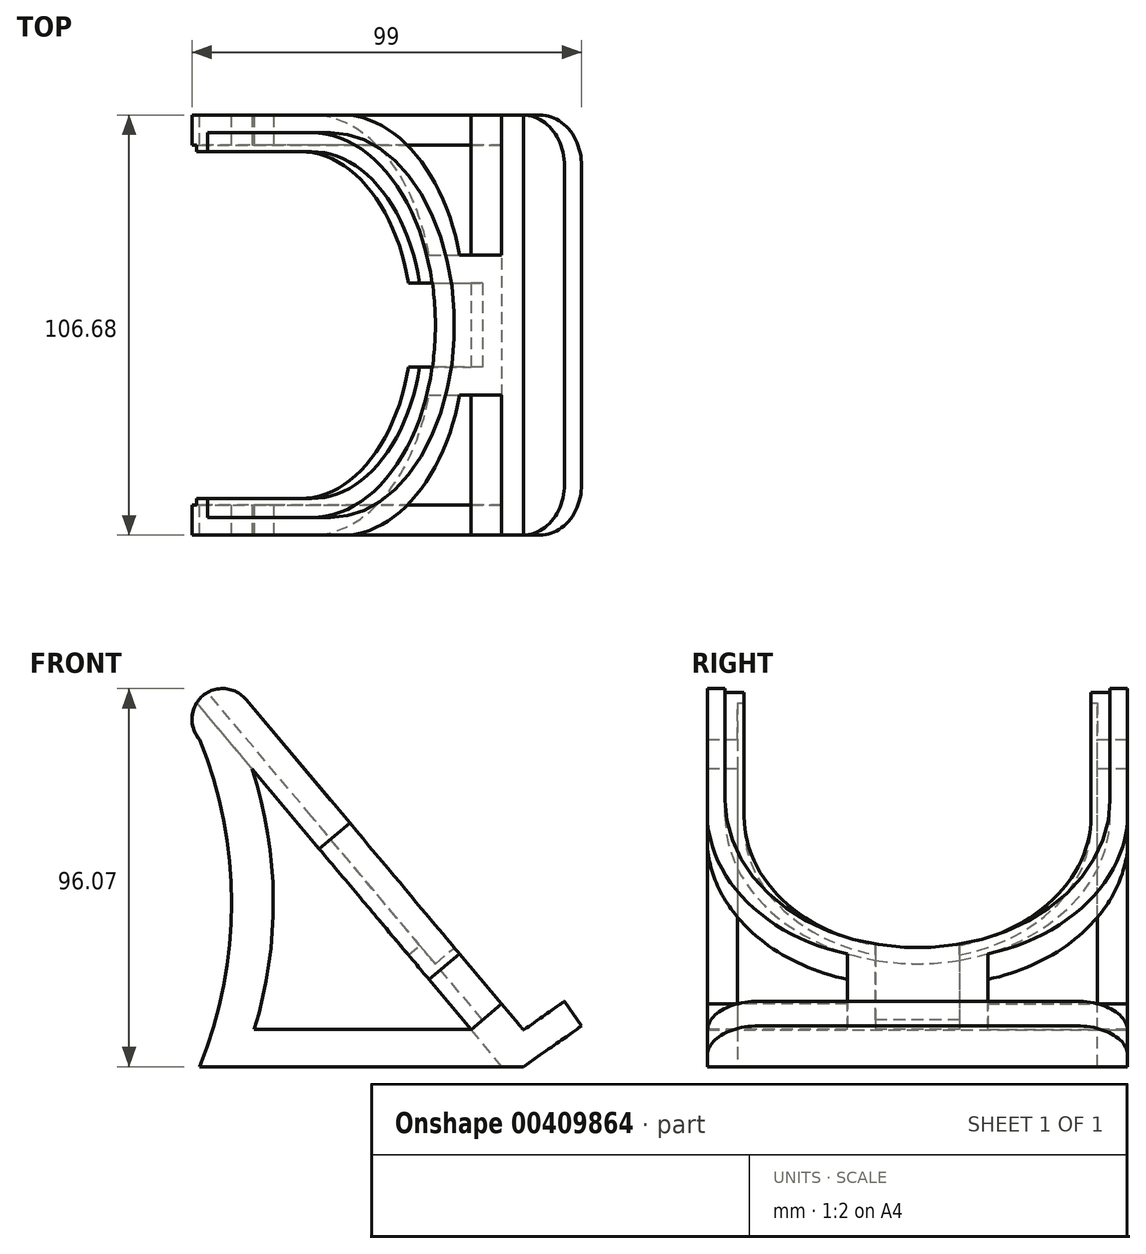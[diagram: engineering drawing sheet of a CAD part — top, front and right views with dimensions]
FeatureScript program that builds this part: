
annotation { "Feature Type Name" : "Feature", "Feature Type Description" : "" }
export const myFeature = defineFeature(function(context is Context, id is Id, definition is map)
    precondition{}
    {
        {
            var Q0;
            Q0=qCreatedBy(makeId("Front.planeOp"),FACE);
            var sketch = newSketch(context, id + "F0", { "sketchPlane" : qUnion([Q0])});
            skLineSegment(sketch, "E0", {"start": v(-26.46, -52) * mm, "end": v(55.88, -52) * mm});
            skLineSegment(sketch, "E1", {"start": v(55.88, -52) * mm, "end": v(70.65, -41.63) * mm});
            skLineSegment(sketch, "E2", {"start": v(70.65, -41.63) * mm, "end": v(66.27, -35.4) * mm});
            skLineSegment(sketch, "E3", {"start": v(66.27, -35.4) * mm, "end": v(55.88, -42.68) * mm});
            skLineSegment(sketch, "E4", {"start": v(55.88, -42.68) * mm, "end": v(-14.6, 41.3) * mm});
            skArc(sketch, "E5", {"start": v(-26.46, -52) * mm, "mid": v(-18.29, -10.4) * mm, "end": v(-26.46, 31.2) * mm});
            skArc(sketch, "E6", {"start": v(-14.6, 41.3) * mm, "mid": v(-25.6, 42.22) * mm, "end": v(-26.46, 31.2) * mm});
            skSolve(sketch);
        }
        {
            var Q0;
            Q0=makeQuery(id+"F0.imprint","IMPRINT",FACE,{"disambiguationData":[TD([[makeQuery(id+"F0.imprint","IMPRINT",EDGE,{"derivedFrom":sQuery(id+"F0.wireOp",EDGE,"E0")}),1.0]])]});
            var Q1;
            Q1=qSketchRegion(id+"F2",true);
            extrude(context, id + "F1", {"entities" : qUnion([Q0, Q1]), "endBound" : BoundingType.SYMMETRIC, "depth" : 106.68 * mm});
        }
        {
            var Q0;
            Q0=makeQuery(id+"F1.opExtrude","SWEPT_FACE",FACE,{"disambiguationData":[OSD([sQuery(id+"F0.wireOp",EDGE,"E4")])]});
            var sketch = newSketch(context, id + "F2", { "sketchPlane" : qUnion([Q0])});
            skCircle(sketch, "E7", {"center": v(0, 7.58) * mm, "radius": 48.9 * mm});
            skLineSegment(sketch, "E8", {"start": v(0, 7.58) * mm, "end": v(-48.9, 7.58) * mm, "construction": true});
            skLineSegment(sketch, "E9", {"start": v(-48.9, 7.58) * mm, "end": v(-48.9, 73.2) * mm});
            skLineSegment(sketch, "E10", {"start": v(-48.9, 73.2) * mm, "end": v(0, 73.2) * mm});
            skLineSegment(sketch, "E11", {"start": v(0, 73.2) * mm, "end": v(0, 7.58) * mm});
            skLineSegment(sketch, "E12", {"start": v(-48.9, 7.58) * mm, "end": v(0, 7.58) * mm});
            skLineSegment(sketch, "E13.MirrorCS", {"start": v(46.05, 73.08) * mm, "end": v(0, 73.2) * mm});
            skLineSegment(sketch, "E14", {"start": v(-6.35, -68.84) * mm, "end": v(6.35, -68.84) * mm});
            skCircle(sketch, "E15", {"center": v(0, 7.58) * mm, "radius": 44.07 * mm});
            skLineSegment(sketch, "E16", {"start": v(-44.07, 7.58) * mm, "end": v(-44.07, 73.2) * mm});
            skLineSegment(sketch, "E17.MirrorCS", {"start": v(44.07, 7.58) * mm, "end": v(44.07, 73.2) * mm});
            skArc(sketch, "E18", {"start": v(-53.34, 0) * mm, "mid": v(-42.03, -27.71) * mm, "end": v(-16.69, -43.64) * mm});
            skLineSegment(sketch, "E19", {"start": v(-17.83, -43.33) * mm, "end": v(-17.83, -59.96) * mm});
            skLineSegment(sketch, "E20", {"start": v(-17.83, -59.96) * mm, "end": v(-53.34, -59.96) * mm});
            skLineSegment(sketch, "E21", {"start": v(-53.34, -59.96) * mm, "end": v(-53.34, 0) * mm});
            skArc(sketch, "E22.MirrorCS", {"start": v(53.34, 0) * mm, "mid": v(42.03, -27.71) * mm, "end": v(16.69, -43.64) * mm});
            skLineSegment(sketch, "E23.MirrorCS", {"start": v(17.83, -43.33) * mm, "end": v(17.83, -59.96) * mm});
            skLineSegment(sketch, "E24.MirrorCS", {"start": v(17.83, -59.96) * mm, "end": v(53.34, -59.96) * mm});
            skLineSegment(sketch, "E25.MirrorCS", {"start": v(53.34, -59.96) * mm, "end": v(53.34, 0) * mm});
            skLineSegment(sketch, "E26.MirrorCS", {"start": v(48.9, 7.58) * mm, "end": v(48.9, 73.2) * mm});
            skLineSegment(sketch, "E27.MirrorCS", {"start": v(48.9, 73.2) * mm, "end": v(0, 73.2) * mm});
            skSolve(sketch);
        }
        {
            var Q0;
            {var subQ1=sQuery(id+"F2.wireOp",EDGE,"E7");var subQ3=sQuery(id+"F2.wireOp",EDGE,"E16");var subQ4=makeQuery(id+"F2.imprint","INTERSECT",VERTEX,{"derivedFrom":[subQ1,subQ3]});Q0=makeQuery(id+"F2.imprint","IMPRINT",FACE,{"disambiguationData":[TD([[makeQuery(id+"F2.imprint","IMPRINT",EDGE,{"disambiguationData":[TD([[subQ4,-1.0]])],"derivedFrom":subQ1}),1.0]])]});}
            var Q1;
            {var subQ0=sQuery(id+"F2.wireOp",EDGE,"E17.MirrorCS");var subQ1=sQuery(id+"F2.wireOp",EDGE,"E7");var subQ2=makeQuery(id+"F2.imprint","INTERSECT",VERTEX,{"derivedFrom":[subQ1,subQ0]});Q1=makeQuery(id+"F2.imprint","IMPRINT",FACE,{"disambiguationData":[TD([[makeQuery(id+"F2.imprint","IMPRINT",EDGE,{"disambiguationData":[TD([[subQ2,1.0]])],"derivedFrom":subQ1}),-1.0]])]});}
            var Q2;
            {var subQ0=sQuery(id+"F2.wireOp",EDGE,"E11");var subQ3=sQuery(id+"F2.wireOp",EDGE,"E7");var subQ4=makeQuery(id+"F2.imprint","INTERSECT",VERTEX,{"derivedFrom":[subQ3,subQ0]});Q2=makeQuery(id+"F2.imprint","IMPRINT",FACE,{"disambiguationData":[TD([[makeQuery(id+"F2.imprint","IMPRINT",EDGE,{"disambiguationData":[TD([[subQ4,-1.0]])],"derivedFrom":subQ3}),-1.0]])]});}
            var Q3;
            {var subQ0=sQuery(id+"F2.wireOp",EDGE,"E10");var subQ1=sQuery(id+"F2.wireOp",EDGE,"E9");var subQ2=makeQuery(id+"F2.imprint","INTERSECT",VERTEX,{"derivedFrom":[subQ1,subQ0]});Q3=makeQuery(id+"F2.imprint","IMPRINT",FACE,{"disambiguationData":[TD([[makeQuery(id+"F2.imprint","IMPRINT",EDGE,{"disambiguationData":[TD([[subQ2,-1.0]])],"derivedFrom":subQ0}),-1.0]])]});}
            var Q4;
            {var subQ0=sQuery(id+"F2.wireOp",EDGE,"E13.MirrorCS");var subQ1=sQuery(id+"F2.wireOp",EDGE,"4d85ec23-4223-449c-91b3-d977c7df0c140.MirrorCS");var subQ2=makeQuery(id+"F2.imprint","INTERSECT",VERTEX,{"derivedFrom":[subQ1,subQ0]});Q4=makeQuery(id+"F2.imprint","IMPRINT",FACE,{"disambiguationData":[TD([[makeQuery(id+"F2.imprint","IMPRINT",EDGE,{"disambiguationData":[TD([[subQ2,-1.0]])],"derivedFrom":subQ0}),1.0]])]});}
            var Q5;
            {var subQ0=sQuery(id+"F2.wireOp",EDGE,"E11");var subQ1=sQuery(id+"F2.wireOp",EDGE,"E7");var subQ2=makeQuery(id+"F2.imprint","INTERSECT",VERTEX,{"derivedFrom":[subQ1,subQ0]});Q5=makeQuery(id+"F2.imprint","IMPRINT",FACE,{"disambiguationData":[TD([[makeQuery(id+"F2.imprint","IMPRINT",EDGE,{"disambiguationData":[TD([[subQ2,-1.0]])],"derivedFrom":subQ1}),1.0]])]});}
            var Q6;
            {var subQ0=sQuery(id+"F2.wireOp",EDGE,"E11");var subQ1=sQuery(id+"F2.wireOp",EDGE,"E7");var subQ2=makeQuery(id+"F2.imprint","INTERSECT",VERTEX,{"derivedFrom":[subQ1,subQ0]});Q6=makeQuery(id+"F2.imprint","IMPRINT",FACE,{"disambiguationData":[TD([[makeQuery(id+"F2.imprint","IMPRINT",EDGE,{"disambiguationData":[TD([[subQ2,1.0]])],"derivedFrom":subQ1}),1.0]])]});}
            var Q7;
            {var subQ1=sQuery(id+"F2.wireOp",EDGE,"E7");var subQ3=sQuery(id+"F2.wireOp",EDGE,"E16");var subQ4=makeQuery(id+"F2.imprint","INTERSECT",VERTEX,{"derivedFrom":[subQ1,subQ3]});Q7=makeQuery(id+"F2.imprint","IMPRINT",FACE,{"disambiguationData":[TD([[makeQuery(id+"F2.imprint","IMPRINT",EDGE,{"disambiguationData":[TD([[subQ4,-1.0]])],"derivedFrom":subQ1}),-1.0]])]});}
            var Q8;
            {var subQ5=sQuery(id+"F2.wireOp",EDGE,"E11");var subQ7=sQuery(id+"F2.wireOp",EDGE,"E7");var subQ8=makeQuery(id+"F2.imprint","INTERSECT",VERTEX,{"derivedFrom":[subQ7,subQ5]});Q8=makeQuery(id+"F2.imprint","IMPRINT",FACE,{"disambiguationData":[TD([[makeQuery(id+"F2.imprint","IMPRINT",EDGE,{"disambiguationData":[TD([[subQ8,1.0]])],"derivedFrom":subQ7}),-1.0]])]});}
            var Q9;
            {var subQ0=sQuery(id+"F2.wireOp",EDGE,"E16");var subQ1=sQuery(id+"F2.wireOp",EDGE,"E7");var subQ2=makeQuery(id+"F2.imprint","INTERSECT",VERTEX,{"derivedFrom":[subQ1,subQ0]});Q9=makeQuery(id+"F2.imprint","IMPRINT",FACE,{"disambiguationData":[TD([[makeQuery(id+"F2.imprint","IMPRINT",EDGE,{"disambiguationData":[TD([[subQ2,1.0]])],"derivedFrom":subQ1}),-1.0]])]});}
            var Q10;
            {var subQ0=sQuery(id+"F2.wireOp",EDGE,"E16");var subQ3=sQuery(id+"F2.wireOp",EDGE,"E7");var subQ4=makeQuery(id+"F2.imprint","INTERSECT",VERTEX,{"derivedFrom":[subQ3,subQ0]});Q10=makeQuery(id+"F2.imprint","IMPRINT",FACE,{"disambiguationData":[TD([[makeQuery(id+"F2.imprint","IMPRINT",EDGE,{"disambiguationData":[TD([[subQ4,1.0]])],"derivedFrom":subQ3}),1.0]])]});}
            var Q11;
            {var subQ0=sQuery(id+"F2.wireOp",EDGE,"E17.MirrorCS");var subQ1=sQuery(id+"F2.wireOp",EDGE,"E15");var subQ2=makeQuery(id+"F2.imprint","INTERSECT",VERTEX,{"derivedFrom":[subQ1,subQ0]});Q11=makeQuery(id+"F2.imprint","IMPRINT",FACE,{"disambiguationData":[TD([[makeQuery(id+"F2.imprint","IMPRINT",EDGE,{"disambiguationData":[TD([[subQ2,-1.0]])],"derivedFrom":subQ1}),-1.0]])]});}
            var Q12;
            {var subQ0=sQuery(id+"F2.wireOp",EDGE,"E7");var subQ7=sQuery(id+"F2.wireOp",EDGE,"E17.MirrorCS");var subQ11=makeQuery(id+"F2.imprint","INTERSECT",VERTEX,{"derivedFrom":[subQ0,subQ7]});Q12=makeQuery(id+"F2.imprint","IMPRINT",FACE,{"disambiguationData":[TD([[makeQuery(id+"F2.imprint","IMPRINT",EDGE,{"disambiguationData":[TD([[subQ11,1.0]])],"derivedFrom":subQ0}),1.0]])]});}
            var Q13;
            {var subQ0=sQuery(id+"F2.wireOp",EDGE,"E12");var subQ1=sQuery(id+"F2.wireOp",EDGE,"E11");var subQ2=makeQuery(id+"F2.imprint","INTERSECT",VERTEX,{"derivedFrom":[subQ1,subQ0]});Q13=makeQuery(id+"F2.imprint","IMPRINT",FACE,{"disambiguationData":[TD([[makeQuery(id+"F2.imprint","IMPRINT",EDGE,{"disambiguationData":[TD([[subQ2,1.0]])],"derivedFrom":subQ1}),1.0]])]});}
            var Q14;
            {var subQ0=sQuery(id+"F2.wireOp",EDGE,"E12");var subQ1=sQuery(id+"F2.wireOp",EDGE,"E11");var subQ2=makeQuery(id+"F2.imprint","INTERSECT",VERTEX,{"derivedFrom":[subQ1,subQ0]});Q14=makeQuery(id+"F2.imprint","IMPRINT",FACE,{"disambiguationData":[TD([[makeQuery(id+"F2.imprint","IMPRINT",EDGE,{"disambiguationData":[TD([[subQ2,1.0]])],"derivedFrom":subQ1}),-1.0]])]});}
            var Q15;
            {var subQ0=sQuery(id+"F2.wireOp",EDGE,"E17.MirrorCS");var subQ1=sQuery(id+"F2.wireOp",EDGE,"E7");var subQ2=makeQuery(id+"F2.imprint","INTERSECT",VERTEX,{"derivedFrom":[subQ1,subQ0]});Q15=makeQuery(id+"F2.imprint","IMPRINT",FACE,{"disambiguationData":[TD([[makeQuery(id+"F2.imprint","IMPRINT",EDGE,{"disambiguationData":[TD([[subQ2,-1.0]])],"derivedFrom":subQ1}),-1.0]])]});}
            var Q16;
            {var subQ0=sQuery(id+"F2.wireOp",EDGE,"E27.MirrorCS");var subQ1=sQuery(id+"F2.wireOp",EDGE,"E17.MirrorCS");var subQ2=makeQuery(id+"F2.imprint","INTERSECT",VERTEX,{"derivedFrom":[subQ1,subQ0]});Q16=makeQuery(id+"F2.imprint","IMPRINT",FACE,{"disambiguationData":[TD([[makeQuery(id+"F2.imprint","IMPRINT",EDGE,{"disambiguationData":[TD([[subQ2,1.0]])],"derivedFrom":subQ1}),-1.0]])]});}
            extrude(context, id + "F3", {"entities" : qUnion([Q0, Q1, Q2, Q3, Q4, Q5, Q6, Q7, Q8, Q9, Q10, Q11, Q12, Q13, Q14, Q15, Q16]), "operationType" : NewBodyOperationType.REMOVE, "oppositeDirection" : true, "depth" : 6.35 * mm});
        }
        {
            var Q0;
            Q0=makeQuery(id+"F1.opExtrude","CAP_FACE",FACE,{"disambiguationData":[OSD([sQuery(id+"F0.wireOp",EDGE,"E0"),sQuery(id+"F0.wireOp",EDGE,"E1"),sQuery(id+"F0.wireOp",EDGE,"E2"),sQuery(id+"F0.wireOp",EDGE,"E3"),sQuery(id+"F0.wireOp",EDGE,"E4"),sQuery(id+"F0.wireOp",EDGE,"E5"),sQuery(id+"F0.wireOp",EDGE,"E6")])],"isStart":false});
            var sketch = newSketch(context, id + "F4", { "sketchPlane" : qUnion([Q0])});
            skLineSegment(sketch, "E28", {"start": v(-13.05, 23.66) * mm, "end": v(42.5, -42.55) * mm});
            skArc(sketch, "E29", {"start": v(-12.51, -42.55) * mm, "mid": v(-7.68, -9.4) * mm, "end": v(-13.05, 23.66) * mm});
            skLineSegment(sketch, "E30", {"start": v(-12.51, -42.55) * mm, "end": v(42.5, -42.55) * mm});
            skSolve(sketch);
        }
        {
            var Q0;
            Q0=makeQuery(id+"F4.imprint","IMPRINT",FACE,{"disambiguationData":[TD([[makeQuery(id+"F4.imprint","IMPRINT",EDGE,{"derivedFrom":sQuery(id+"F4.wireOp",EDGE,"E28")}),-1.0]])]});
            var Q1;
            Q1=makeQuery(id+"F4.imprint","IMPRINT",FACE,{"disambiguationData":[TD([[makeQuery(id+"F4.imprint","IMPRINT",EDGE,{"derivedFrom":sQuery(id+"F4.wireOp",EDGE,"wPjwQzWi-Tjyw-v6FZ-FHt0-rqqnCeeGMehr")}),-1.0]])]});
            extrude(context, id + "F5", {"entities" : qUnion([Q0, Q1]), "operationType" : NewBodyOperationType.REMOVE, "endBound" : BoundingType.UP_TO_NEXT, "oppositeDirection" : true, "depth" : 25.4 * mm});
        }
        {
            var Q0;
            Q0=makeQuery(id+"F1.opExtrude","SWEPT_EDGE",EDGE,{"disambiguationData":[OSD([sQuery(id+"F0.wireOp",EDGE,"E0"),sQuery(id+"F0.wireOp",EDGE,"E5")])]});
            cPlane(context, id + "F6", {"entities" : qUnion([Q0]), "cplaneType" : CPlaneType.LINE_ANGLE, "offset" : 40.4 * mm, "angle" : 50 * degree, "width" : 152.4 * mm, "height" : 152.4 * mm});
        }
        {
            var Q0;
            Q0=qCreatedBy(id+"F6.planeOp",FACE);
            var sketch = newSketch(context, id + "F7", { "sketchPlane" : qUnion([Q0])});
            skLineSegment(sketch, "E31", {"start": v(45.72, 83.56) * mm, "end": v(-45.72, 83.56) * mm});
            skLineSegment(sketch, "E32", {"start": v(-45.72, 83.56) * mm, "end": v(-45.72, -100.06) * mm});
            skLineSegment(sketch, "E33", {"start": v(-45.72, -100.06) * mm, "end": v(45.72, -100.06) * mm});
            skLineSegment(sketch, "E34", {"start": v(45.72, -100.06) * mm, "end": v(45.72, 83.56) * mm});
            skSolve(sketch);
        }
        {
            var Q0;
            Q0=makeQuery(id+"F7.imprint","IMPRINT",FACE,{"disambiguationData":[TD([[makeQuery(id+"F7.imprint","IMPRINT",EDGE,{"derivedFrom":sQuery(id+"F7.wireOp",EDGE,"E31")}),1.0]])]});
            extrude(context, id + "F8", {"entities" : qUnion([Q0]), "operationType" : NewBodyOperationType.REMOVE, "depth" : 58.93 * mm});
        }
        {
            var Q0;
            {var subQ0=sQuery(id+"F2.wireOp",EDGE,"E12");var subQ1=sQuery(id+"F2.wireOp",EDGE,"E11");var subQ2=makeQuery(id+"F2.imprint","INTERSECT",VERTEX,{"derivedFrom":[subQ1,subQ0]});Q0=makeQuery(id+"F2.imprint","IMPRINT",FACE,{"disambiguationData":[TD([[makeQuery(id+"F2.imprint","IMPRINT",EDGE,{"disambiguationData":[TD([[subQ2,1.0]])],"derivedFrom":subQ1}),-1.0]])]});}
            var Q1;
            {var subQ0=sQuery(id+"F2.wireOp",EDGE,"E12");var subQ1=sQuery(id+"F2.wireOp",EDGE,"E11");var subQ2=makeQuery(id+"F2.imprint","INTERSECT",VERTEX,{"derivedFrom":[subQ1,subQ0]});Q1=makeQuery(id+"F2.imprint","IMPRINT",FACE,{"disambiguationData":[TD([[makeQuery(id+"F2.imprint","IMPRINT",EDGE,{"disambiguationData":[TD([[subQ2,1.0]])],"derivedFrom":subQ1}),1.0]])]});}
            var Q2;
            {var subQ0=sQuery(id+"F2.wireOp",EDGE,"E16");var subQ3=sQuery(id+"F2.wireOp",EDGE,"E7");var subQ4=makeQuery(id+"F2.imprint","INTERSECT",VERTEX,{"derivedFrom":[subQ3,subQ0]});Q2=makeQuery(id+"F2.imprint","IMPRINT",FACE,{"disambiguationData":[TD([[makeQuery(id+"F2.imprint","IMPRINT",EDGE,{"disambiguationData":[TD([[subQ4,1.0]])],"derivedFrom":subQ3}),1.0]])]});}
            var Q3;
            {var subQ0=sQuery(id+"F2.wireOp",EDGE,"E17.MirrorCS");var subQ1=sQuery(id+"F2.wireOp",EDGE,"E15");var subQ2=makeQuery(id+"F2.imprint","INTERSECT",VERTEX,{"derivedFrom":[subQ1,subQ0]});Q3=makeQuery(id+"F2.imprint","IMPRINT",FACE,{"disambiguationData":[TD([[makeQuery(id+"F2.imprint","IMPRINT",EDGE,{"disambiguationData":[TD([[subQ2,-1.0]])],"derivedFrom":subQ1}),-1.0]])]});}
            var Q4;
            {var subQ0=sQuery(id+"F2.wireOp",EDGE,"E11");var subQ1=sQuery(id+"F2.wireOp",EDGE,"E7");var subQ2=makeQuery(id+"F2.imprint","INTERSECT",VERTEX,{"derivedFrom":[subQ1,subQ0]});Q4=makeQuery(id+"F2.imprint","IMPRINT",FACE,{"disambiguationData":[TD([[makeQuery(id+"F2.imprint","IMPRINT",EDGE,{"disambiguationData":[TD([[subQ2,1.0]])],"derivedFrom":subQ1}),1.0]])]});}
            var Q5;
            {var subQ0=sQuery(id+"F2.wireOp",EDGE,"E11");var subQ1=sQuery(id+"F2.wireOp",EDGE,"E7");var subQ2=makeQuery(id+"F2.imprint","INTERSECT",VERTEX,{"derivedFrom":[subQ1,subQ0]});Q5=makeQuery(id+"F2.imprint","IMPRINT",FACE,{"disambiguationData":[TD([[makeQuery(id+"F2.imprint","IMPRINT",EDGE,{"disambiguationData":[TD([[subQ2,-1.0]])],"derivedFrom":subQ1}),1.0]])]});}
            var Q6;
            {var subQ0=sQuery(id+"F2.wireOp",EDGE,"E11");var subQ3=sQuery(id+"F2.wireOp",EDGE,"E7");var subQ4=makeQuery(id+"F2.imprint","INTERSECT",VERTEX,{"derivedFrom":[subQ3,subQ0]});Q6=makeQuery(id+"F2.imprint","IMPRINT",FACE,{"disambiguationData":[TD([[makeQuery(id+"F2.imprint","IMPRINT",EDGE,{"disambiguationData":[TD([[subQ4,-1.0]])],"derivedFrom":subQ3}),-1.0]])]});}
            var Q7;
            {var subQ0=sQuery(id+"F2.wireOp",EDGE,"E16");var subQ1=sQuery(id+"F2.wireOp",EDGE,"E7");var subQ2=makeQuery(id+"F2.imprint","INTERSECT",VERTEX,{"derivedFrom":[subQ1,subQ0]});Q7=makeQuery(id+"F2.imprint","IMPRINT",FACE,{"disambiguationData":[TD([[makeQuery(id+"F2.imprint","IMPRINT",EDGE,{"disambiguationData":[TD([[subQ2,1.0]])],"derivedFrom":subQ1}),-1.0]])]});}
            var Q8;
            {var subQ5=sQuery(id+"F2.wireOp",EDGE,"E11");var subQ7=sQuery(id+"F2.wireOp",EDGE,"E7");var subQ8=makeQuery(id+"F2.imprint","INTERSECT",VERTEX,{"derivedFrom":[subQ7,subQ5]});Q8=makeQuery(id+"F2.imprint","IMPRINT",FACE,{"disambiguationData":[TD([[makeQuery(id+"F2.imprint","IMPRINT",EDGE,{"disambiguationData":[TD([[subQ8,1.0]])],"derivedFrom":subQ7}),-1.0]])]});}
            var Q9;
            {var subQ0=sQuery(id+"F2.wireOp",EDGE,"E17.MirrorCS");var subQ1=sQuery(id+"F2.wireOp",EDGE,"E7");var subQ2=makeQuery(id+"F2.imprint","INTERSECT",VERTEX,{"derivedFrom":[subQ1,subQ0]});Q9=makeQuery(id+"F2.imprint","IMPRINT",FACE,{"disambiguationData":[TD([[makeQuery(id+"F2.imprint","IMPRINT",EDGE,{"disambiguationData":[TD([[subQ2,-1.0]])],"derivedFrom":subQ1}),-1.0]])]});}
            var Q10;
            {var subQ0=sQuery(id+"F2.wireOp",EDGE,"E15");var subQ1=sQuery(id+"F2.wireOp",EDGE,"E11");var subQ2=makeQuery(id+"F2.imprint","INTERSECT",VERTEX,{"derivedFrom":[subQ1,subQ0]});Q10=makeQuery(id+"F2.imprint","IMPRINT",FACE,{"disambiguationData":[TD([[makeQuery(id+"F2.imprint","IMPRINT",EDGE,{"disambiguationData":[TD([[subQ2,-1.0]])],"derivedFrom":subQ1}),1.0]])]});}
            var Q11;
            {var subQ0=sQuery(id+"F2.wireOp",EDGE,"E15");var subQ1=sQuery(id+"F2.wireOp",EDGE,"E11");var subQ2=makeQuery(id+"F2.imprint","INTERSECT",VERTEX,{"derivedFrom":[subQ1,subQ0]});Q11=makeQuery(id+"F2.imprint","IMPRINT",FACE,{"disambiguationData":[TD([[makeQuery(id+"F2.imprint","IMPRINT",EDGE,{"disambiguationData":[TD([[subQ2,-1.0]])],"derivedFrom":subQ1}),-1.0]])]});}
            extrude(context, id + "F9", {"entities" : qUnion([Q0, Q1, Q2, Q3, Q4, Q5, Q6, Q7, Q8, Q9, Q10, Q11]), "operationType" : NewBodyOperationType.REMOVE, "oppositeDirection" : true, "depth" : 25.4 * mm});
        }
        {
            var Q0;
            Q0=makeQuery(id+"F1.opExtrude","CAP_EDGE",EDGE,{"disambiguationData":[OSD([sQuery(id+"F0.wireOp",EDGE,"E2")])],"isStart":false});
            var Q1;
            Q1=makeQuery(id+"F1.opExtrude","CAP_EDGE",EDGE,{"disambiguationData":[OSD([sQuery(id+"F0.wireOp",EDGE,"E2")])],"isStart":true});
            fillet(context, id + "F10", {"entities" : qUnion([Q0, Q1]), "radius" : 12.88 * mm, "tangentPropagation" : true, "allowEdgeOverflow" : false});
        }
        {
            var Q0;
            {var subQ2=sQuery(id+"F2.wireOp",EDGE,"E19");Q0=makeQuery(id+"F2.imprint","IMPRINT",FACE,{"disambiguationData":[TD([[makeQuery(id+"F2.imprint","IMPRINT",EDGE,{"derivedFrom":subQ2}),-1.0]])]});}
            var Q1;
            {var subQ2=sQuery(id+"F2.wireOp",EDGE,"E23.MirrorCS");Q1=makeQuery(id+"F2.imprint","IMPRINT",FACE,{"disambiguationData":[TD([[makeQuery(id+"F2.imprint","IMPRINT",EDGE,{"derivedFrom":subQ2}),1.0]])]});}
            extrude(context, id + "F11", {"entities" : qUnion([Q0, Q1]), "operationType" : NewBodyOperationType.REMOVE, "oppositeDirection" : true, "depth" : 10.16 * mm});
        }
        {
            var Q0;
            Q0=makeQuery(id+"F3.boolean.opBoolean","COPY",FACE,{"derivedFrom":makeQuery(id+"F3.opExtrude","CAP_FACE",FACE,{"disambiguationData":[OSD([sQuery(id+"F0.wireOp",EDGE,"E4"),sQuery(id+"F0.wireOp",EDGE,"E6"),sQuery(id+"F2.wireOp",EDGE,"E7"),sQuery(id+"F2.wireOp",EDGE,"E9"),sQuery(id+"F2.wireOp",EDGE,"E10"),sQuery(id+"F2.wireOp",EDGE,"E13.MirrorCS"),sQuery(id+"F2.wireOp",EDGE,"E15"),sQuery(id+"F2.wireOp",EDGE,"E17.MirrorCS"),sQuery(id+"F2.wireOp",EDGE,"E26.MirrorCS"),sQuery(id+"F2.wireOp",EDGE,"E27.MirrorCS")])],"isStart":false})});
            var sketch = newSketch(context, id + "F12", { "sketchPlane" : qUnion([Q0])});
            skLineSegment(sketch, "E35", {"start": v(-10.66, -35.18) * mm, "end": v(-10.66, -40.13) * mm});
            skLineSegment(sketch, "E36", {"start": v(0, -41.31) * mm, "end": v(0, -36.48) * mm});
            skLineSegment(sketch, "E37.MirrorCS", {"start": v(10.66, -35.18) * mm, "end": v(10.66, -40.13) * mm});
            skSolve(sketch);
        }
        {
            var Q0;
            {var subQ0=sQuery(id+"F12.wireOp",EDGE,"E35");Q0=makeQuery(id+"F12.imprint","IMPRINT",FACE,{"disambiguationData":[TD([[makeQuery(id+"F12.imprint","IMPRINT",EDGE,{"derivedFrom":subQ0}),1.0]])]});}
            var Q1;
            {var subQ0=sQuery(id+"F12.wireOp",EDGE,"E36");Q1=makeQuery(id+"F12.imprint","IMPRINT",FACE,{"disambiguationData":[TD([[makeQuery(id+"F12.imprint","IMPRINT",EDGE,{"derivedFrom":subQ0}),-1.0]])]});}
            extrude(context, id + "F13", {"entities" : qUnion([Q0, Q1]), "operationType" : NewBodyOperationType.REMOVE, "oppositeDirection" : true, "depth" : 25.4 * mm});
        }
        {
            var Q0;
            Q0=makeQuery(id+"F8.boolean.opBoolean","COPY",FACE,{"derivedFrom":makeQuery(id+"F8.opExtrude","CAP_FACE",FACE,{"disambiguationData":[OSD([sQuery(id+"F7.wireOp",EDGE,"E31"),sQuery(id+"F7.wireOp",EDGE,"E32"),sQuery(id+"F7.wireOp",EDGE,"E33"),sQuery(id+"F7.wireOp",EDGE,"E34")])],"isStart":false})});
            var sketch = newSketch(context, id + "F14", { "sketchPlane" : qUnion([Q0])});
            skLineSegment(sketch, "E38", {"start": v(-10.66, -40.13) * mm, "end": v(-10.66, -59.96) * mm});
            skLineSegment(sketch, "E39", {"start": v(-10.66, -59.96) * mm, "end": v(10.66, -59.96) * mm});
            skLineSegment(sketch, "E40", {"start": v(10.66, -59.96) * mm, "end": v(10.66, -40.13) * mm});
            skLineSegment(sketch, "E41", {"start": v(-17.83, -59.96) * mm, "end": v(17.83, -59.96) * mm, "construction": true});
            skSolve(sketch);
        }
        {
            var Q0;
            Q0=makeQuery(id+"F14.imprint","IMPRINT",FACE,{"disambiguationData":[TD([[makeQuery(id+"F14.imprint","IMPRINT",EDGE,{"derivedFrom":sQuery(id+"F14.wireOp",EDGE,"E38")}),1.0]])]});
            extrude(context, id + "F15", {"entities" : qUnion([Q0]), "operationType" : NewBodyOperationType.REMOVE, "oppositeDirection" : true, "depth" : 3.8 * mm});
        }
    });
